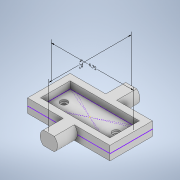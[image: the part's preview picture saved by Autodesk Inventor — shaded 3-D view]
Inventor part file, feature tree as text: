
AUTODESK INVENTOR PART (.ipt)
format: ipt  version: 2021.1 (Build 251245010, 245A)  size: 154,112 bytes
history: native  units: in
note: dims shown in document units (in); Inventor stores cm internally (conversion verified against a paired STEP export)
features: other x3, sketch x3, extrude x3, mirror x1, hole x1
ambient origin geometry x8: Origin, YZ Plane, XZ Plane, XY Plane, X Axis, Y Axis, Z Axis, Center Point
bodies: Solid1 (feature_tree)
feature tree (11):
  other  "Annotations"
  sketch  "Sketch1"  dims[d4=0.375in d5=0.0in]
  extrude  "Extrusion1"  TaperAngle=0.0deg  [1 undecoded]
  extrude  "Extrusion2"  Depth=0.3875in
  extrude  "Extrusion4"  Depth=0.5in
  mirror  "Mirror1"
  hole  "Hole1"  [1 undecoded]
  sketch  "Sketch4"  dims[d7=0.0in d10=0.3875in]
  sketch  "Sketch5"  dims[d13=1.15in d14=0.0in d16=0.5in d17=0.201in d18=0.25in d19=0.4in d20=0.1in d21=0.5635in d22=0.25in d23=0.0in d24=4.75in d25=0.1738in d26=0.0922in d27=4.75in]
  other  "Linear Dimension 1"
  other  "Linear Dimension 2"
note: 2 required parameter values undecoded (feature->parameter linkage not recoverable at this tier; creation-order binding heuristic only, values carry confidence <= 0.55)
